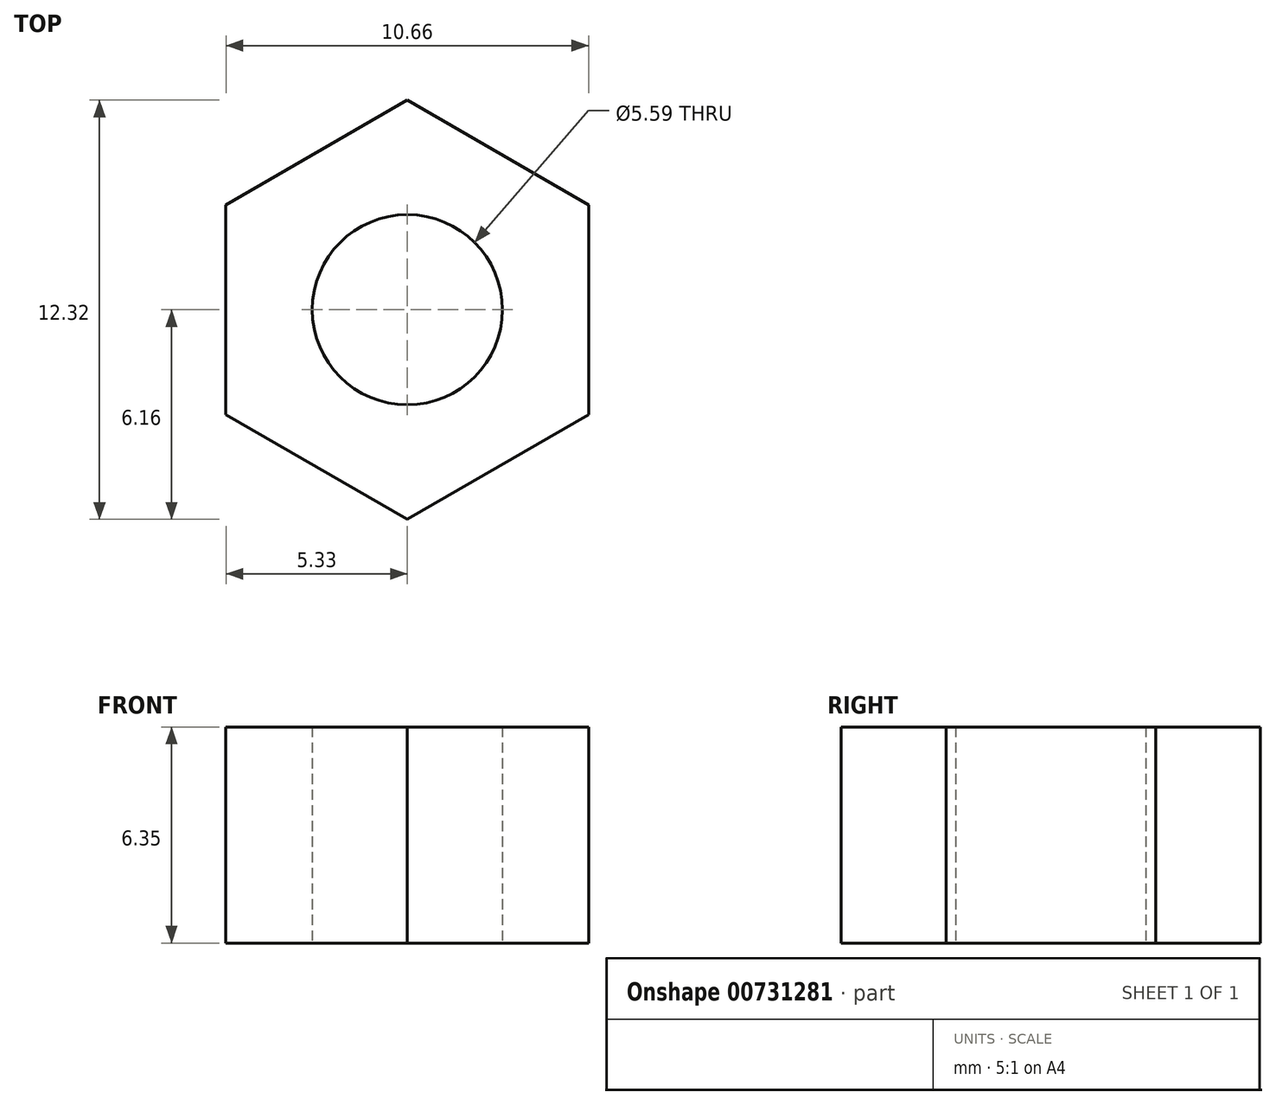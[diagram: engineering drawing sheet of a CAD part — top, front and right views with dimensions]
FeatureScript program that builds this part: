
annotation { "Feature Type Name" : "Feature", "Feature Type Description" : "" }
export const myFeature = defineFeature(function(context is Context, id is Id, definition is map)
    precondition{}
    {
        {
            var Q0;
            Q0=qCreatedBy(makeId("Top.planeOp"),FACE);
            var sketch = newSketch(context, id + "F0", { "sketchPlane" : qUnion([Q0])});
            skCircle(sketch, "E0", {"center": v(0, 0) * mm, "radius": 2.8 * mm});
            skCircle(sketch, "E1.cCircle", {"center": v(0, 0) * mm, "radius": 5.33 * mm, "construction": true});
            skLineSegment(sketch, "E1.0", {"start": v(5.33, -3.08) * mm, "end": v(0, -6.16) * mm});
            skLineSegment(sketch, "E1.1", {"start": v(0, -6.16) * mm, "end": v(-5.33, -3.08) * mm});
            skLineSegment(sketch, "E1.2", {"start": v(-5.33, -3.08) * mm, "end": v(-5.33, 3.08) * mm});
            skLineSegment(sketch, "E1.3", {"start": v(-5.33, 3.08) * mm, "end": v(0, 6.16) * mm});
            skLineSegment(sketch, "E1.4", {"start": v(0, 6.16) * mm, "end": v(5.33, 3.08) * mm});
            skLineSegment(sketch, "E1.5", {"start": v(5.33, 3.08) * mm, "end": v(5.33, -3.08) * mm});
            skPoint(sketch, "E1.0.midPoint", {"position": v(2.67, -4.62) * mm});
            skSolve(sketch);
        }
        {
            var Q0;
            Q0 = qSketchRegion(id + "F0", true);
            extrude(context, id + "F1", {"entities" : qUnion([Q0]), "depth" : 6.35 * mm, "offsetDistance" : 25.4 * mm});
        }
    });
